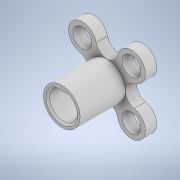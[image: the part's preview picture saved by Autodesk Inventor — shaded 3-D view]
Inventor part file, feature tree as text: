
AUTODESK INVENTOR PART (.ipt)
format: ipt  version: 2020 (Build 240168000, 168)  size: 201,216 bytes
history: native  units: in
note: dims shown in document units (in); Inventor stores cm internally (conversion verified against a paired STEP export)
features: extrude x3, sketch x3, projected_geometry x2, chamfer x1
ambient origin geometry x8: Origin, YZ Plane, XZ Plane, XY Plane, X Axis, Y Axis, Z Axis, Center Point
bodies: Solid1 (feature_tree)
feature tree (9):
  extrude  "Extrusion1"  Depth=0.9843in
  extrude  "Extrusion2"  Depth=0.1969in
  extrude  "Extrusion3"  Depth=0.1181in
  chamfer  "Chamfer1"  Distance=0.1181in
  sketch  "Sketch1"  dims[d0=0.25in d1=0.9843in]
  sketch  "Sketch2"  dims[d2=0.2283in d3=0.1969in]
  projected_geometry  "Projected Loop1"
  sketch  "Sketch3"  dims[d6=0.5118in d7=0.0197in d8=0.1181in d9=0.0in d12=0.0472in d13=0.0472in d14=0.0625in d15=0.0in d16=0.4724in d17=0.0in d18=0.0197in d19=0.125in d20=45.0deg]
  projected_geometry  "Projected Loop2"
